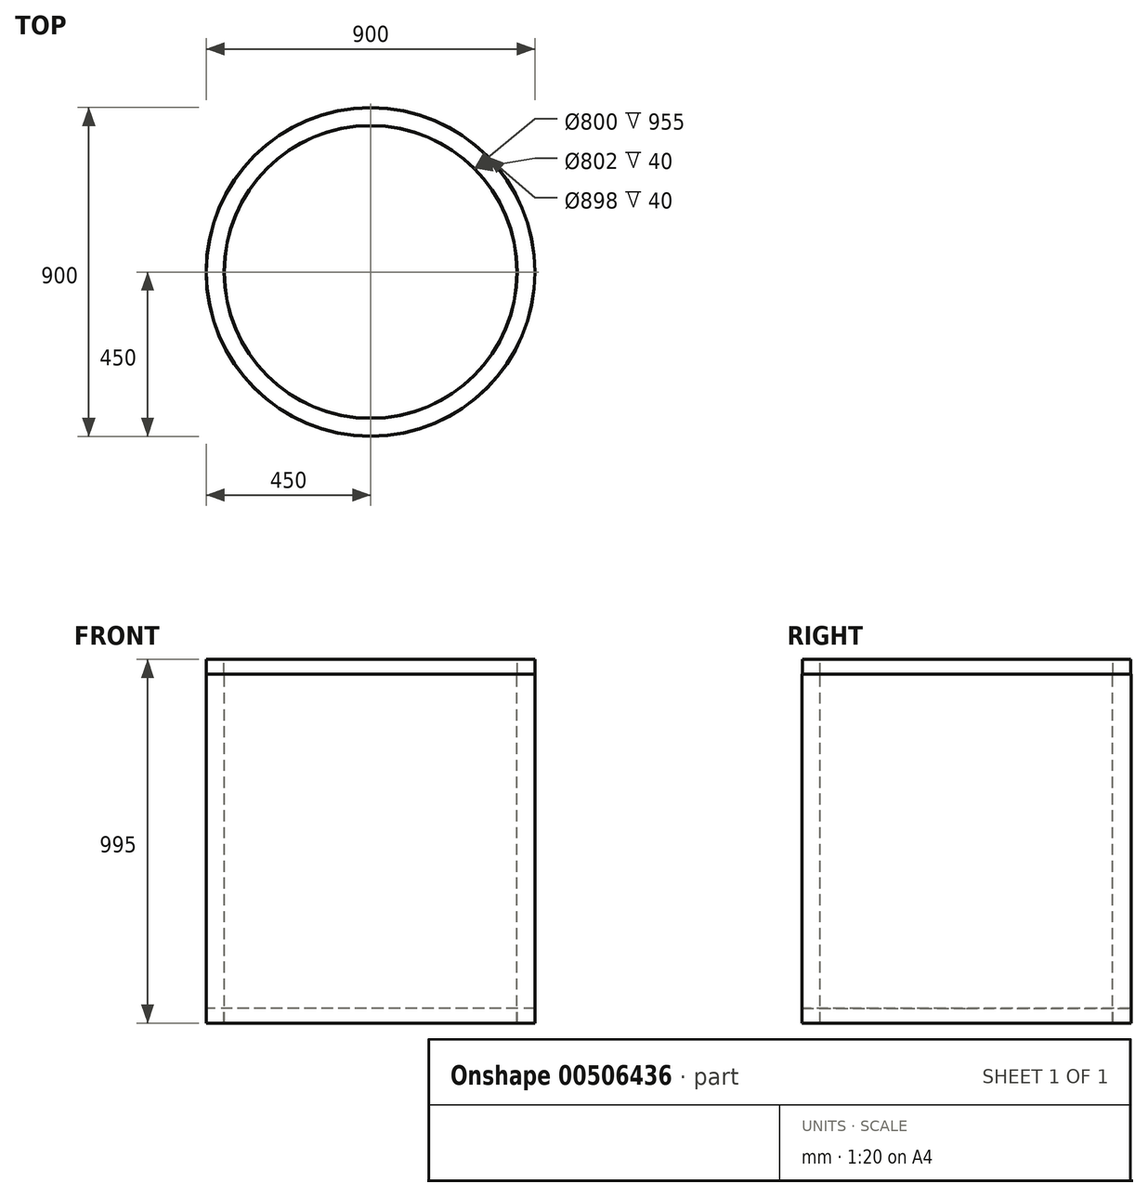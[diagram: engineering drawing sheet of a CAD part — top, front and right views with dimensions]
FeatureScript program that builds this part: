
annotation { "Feature Type Name" : "Feature", "Feature Type Description" : "" }
export const myFeature = defineFeature(function(context is Context, id is Id, definition is map)
    precondition{}
    {
        {
            var Q0;
            Q0=qCreatedBy(makeId("Front.planeOp"),FACE);
            var sketch = newSketch(context, id + "F0", { "sketchPlane" : qUnion([Q0])});
            skLineSegment(sketch, "E0", {"start": v(0, 452.89) * mm, "end": v(0, -450.9) * mm, "construction": true});
            skLineSegment(sketch, "E1", {"start": v(-400, -411.7) * mm, "end": v(-400, 543.3) * mm});
            skLineSegment(sketch, "E2", {"start": v(-400, 543.3) * mm, "end": v(-401, 543.3) * mm});
            skLineSegment(sketch, "E3", {"start": v(-401, 543.3) * mm, "end": v(-401, 583.3) * mm});
            skLineSegment(sketch, "E4", {"start": v(-401, 583.3) * mm, "end": v(-449, 583.3) * mm});
            skLineSegment(sketch, "E5", {"start": v(-449, 583.3) * mm, "end": v(-449, 543.3) * mm});
            skLineSegment(sketch, "E6", {"start": v(-449, 543.3) * mm, "end": v(-450, 543.3) * mm});
            skLineSegment(sketch, "E7", {"start": v(-450, 543.3) * mm, "end": v(-450, -411.7) * mm});
            skLineSegment(sketch, "E8", {"start": v(-450, -411.7) * mm, "end": v(-449, -411.7) * mm});
            skLineSegment(sketch, "E9", {"start": v(-449, -411.7) * mm, "end": v(-449, -371.7) * mm});
            skLineSegment(sketch, "E10", {"start": v(-449, -371.7) * mm, "end": v(-401, -371.7) * mm});
            skLineSegment(sketch, "E11", {"start": v(-401, -371.7) * mm, "end": v(-401, -411.7) * mm});
            skLineSegment(sketch, "E12", {"start": v(-401, -411.7) * mm, "end": v(-400, -411.7) * mm});
            skSolve(sketch);
        }
        {
            var Q0;
            Q0=qSketchRegion(id+"F0",true);
            var Q1;
            Q1=sQuery(id+"F0.wireOp",EDGE,"E0");
            revolve(context, id + "F1", {"entities" : qUnion([Q0]), "axis" : qUnion([Q1]), "revolveType" : RevolveType.FULL});
        }
    });
